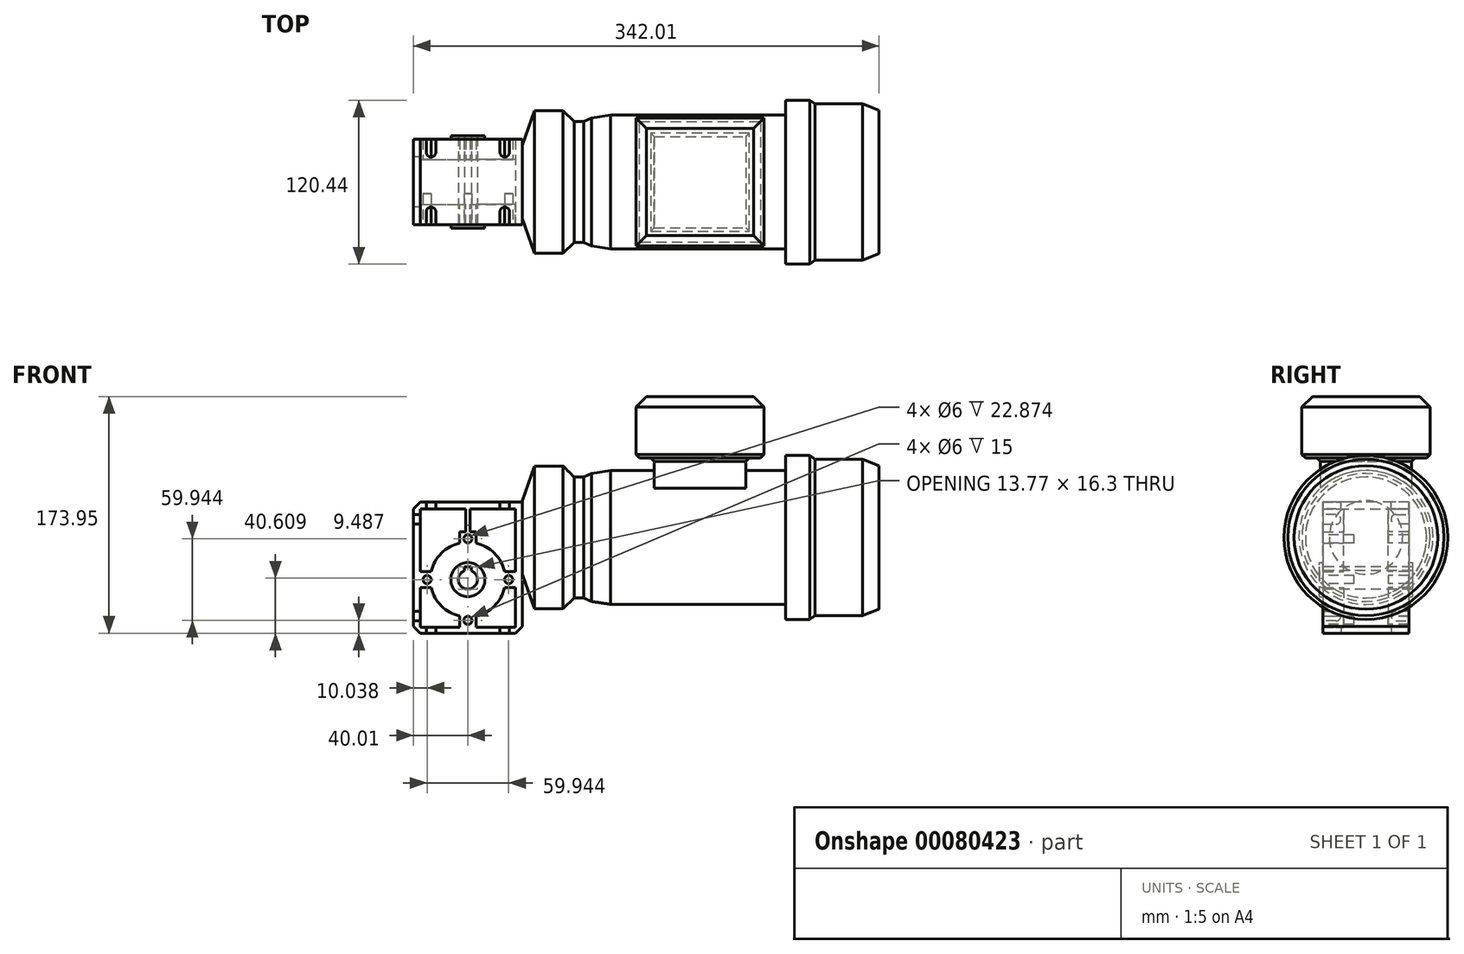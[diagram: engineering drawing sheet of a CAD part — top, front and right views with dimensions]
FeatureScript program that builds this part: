
annotation { "Feature Type Name" : "Feature", "Feature Type Description" : "" }
export const myFeature = defineFeature(function(context is Context, id is Id, definition is map)
    precondition{}
    {
        {
            var Q0;
            Q0=qCreatedBy(makeId("Top.planeOp"),FACE);
            var sketch = newSketch(context, id + "F0", { "sketchPlane" : qUnion([Q0])});
            skLineSegment(sketch, "E0.bottom", {"start": v(-40, 16.5) * mm, "end": v(40, 16.5) * mm});
            skLineSegment(sketch, "E0.top", {"start": v(-40, -16.5) * mm, "end": v(40, -16.5) * mm});
            skLineSegment(sketch, "E0.left", {"start": v(-40, 16.5) * mm, "end": v(-40, -16.5) * mm});
            skLineSegment(sketch, "E0.right", {"start": v(40, 16.5) * mm, "end": v(40, -16.5) * mm});
            skPoint(sketch, "E0.middle", {"position": v(0, 0) * mm});
            skSolve(sketch);
        }
        {
            var Q0;
            Q0 = qSketchRegion(id + "F0", true);
            extrude(context, id + "F1", {"entities" : qUnion([Q0]), "endBound" : BoundingType.SYMMETRIC, "depth" : 96.35 * mm});
        }
        {
            var Q0;
            Q0=makeQuery(id+"F1.opExtrude","SWEPT_FACE",FACE,{"disambiguationData":[OSD([sQuery(id+"F0.wireOp",EDGE,"E0.top")])]});
            var sketch = newSketch(context, id + "F2", { "sketchPlane" : qUnion([Q0])});
            skArc(sketch, "E1", {"start": v(-2.5, -2.18) * mm, "mid": v(0, -15.72) * mm, "end": v(2.5, -2.18) * mm});
            skLineSegment(sketch, "E2", {"start": v(-2.5, -2.18) * mm, "end": v(-2.5, 0.58) * mm});
            skLineSegment(sketch, "E3", {"start": v(-2.5, 0.58) * mm, "end": v(2.5, 0.58) * mm});
            skLineSegment(sketch, "E4", {"start": v(2.5, 0.58) * mm, "end": v(2.5, -2.18) * mm});
            skPoint(sketch, "E5", {"position": v(0, -15.72) * mm});
            skSolve(sketch);
        }
        {
            var Q0;
            Q0 = qSketchRegion(id + "F2", true);
            extrude(context, id + "F3", {"entities" : qUnion([Q0]), "operationType" : NewBodyOperationType.REMOVE, "endBound" : BoundingType.UP_TO_NEXT, "oppositeDirection" : true, "depth" : 25.4 * mm});
        }
        {
            var Q0;
            Q0=qCreatedBy(makeId("Front.planeOp"),FACE);
            var sketch = newSketch(context, id + "F4", { "sketchPlane" : qUnion([Q0])});
            skCircle(sketch, "E6", {"center": v(0, -8.72) * mm, "radius": 12.5 * mm});
            skArc(sketch, "E7.0", {"start": v(-2.5, -2.18) * mm, "mid": v(0, -15.72) * mm, "end": v(2.5, -2.18) * mm});
            skLineSegment(sketch, "E8.0", {"start": v(2.5, 0.58) * mm, "end": v(2.5, -2.18) * mm});
            skLineSegment(sketch, "E9.0", {"start": v(-2.5, 0.58) * mm, "end": v(2.5, 0.58) * mm});
            skLineSegment(sketch, "E10.0", {"start": v(-2.5, -2.18) * mm, "end": v(-2.5, 0.58) * mm});
            skSolve(sketch);
        }
        {
            var Q0;
            Q0 = qSketchRegion(id + "F4", true);
            extrude(context, id + "F5", {"entities" : qUnion([Q0]), "operationType" : NewBodyOperationType.ADD, "endBound" : BoundingType.SYMMETRIC, "depth" : 68.07 * mm});
        }
        {
            var Q0;
            Q0=makeQuery(id+"F1.opExtrude","SWEPT_FACE",FACE,{"disambiguationData":[OSD([sQuery(id+"F0.wireOp",EDGE,"E0.top")])]});
            var sketch = newSketch(context, id + "F6", { "sketchPlane" : qUnion([Q0])});
            skCircle(sketch, "E11", {"center": v(0, 21.25) * mm, "radius": 3 * mm});
            skPoint(sketch, "E12", {"position": v(0, -8.72) * mm});
            skCircle(sketch, "E13.1.0", {"center": v(-29.97, -8.72) * mm, "radius": 3 * mm});
            skCircle(sketch, "E13.2.0", {"center": v(0, -38.7) * mm, "radius": 3 * mm});
            skCircle(sketch, "E13.3.0", {"center": v(29.97, -8.72) * mm, "radius": 3 * mm});
            skSolve(sketch);
        }
        {
            var Q0;
            Q0 = qSketchRegion(id + "F6", true);
            extrude(context, id + "F7", {"entities" : qUnion([Q0]), "operationType" : NewBodyOperationType.REMOVE, "oppositeDirection" : true, "depth" : 7.87 * mm});
        }
        {
            var Q0;
            Q0=makeQuery(id+"F1.opExtrude","SWEPT_FACE",FACE,{"disambiguationData":[OSD([sQuery(id+"F0.wireOp",EDGE,"E0.top")])]});
            var sketch = newSketch(context, id + "F8", { "sketchPlane" : qUnion([Q0])});
            skLineSegment(sketch, "E14", {"start": v(-6, 18.12) * mm, "end": v(-6, 26.28) * mm});
            skLineSegment(sketch, "E15", {"start": v(-6, 26.28) * mm, "end": v(6, 26.28) * mm});
            skLineSegment(sketch, "E16", {"start": v(6, 26.28) * mm, "end": v(6, 18.12) * mm});
            skArc(sketch, "E17", {"start": v(-6, 18.12) * mm, "mid": v(-19.45, 10.72) * mm, "end": v(-26.84, -2.72) * mm});
            skArc(sketch, "E18", {"start": v(6, 18.12) * mm, "mid": v(0, 18.78) * mm, "end": v(-6, 18.12) * mm, "construction": true});
            skLineSegment(sketch, "E19", {"start": v(-6, -35.56) * mm, "end": v(-6, -35.56) * mm});
            skLineSegment(sketch, "E20", {"start": v(-6, -43.72) * mm, "end": v(6, -43.72) * mm});
            skLineSegment(sketch, "E21", {"start": v(6, -43.72) * mm, "end": v(6, -35.56) * mm});
            skLineSegment(sketch, "E22", {"start": v(-6, -35.56) * mm, "end": v(-6, -43.72) * mm});
            skArc(sketch, "E23", {"start": v(-6, -35.56) * mm, "mid": v(0, -36.22) * mm, "end": v(6, -35.56) * mm, "construction": true});
            skArc(sketch, "E24", {"start": v(6, -35.56) * mm, "mid": v(19.45, -28.17) * mm, "end": v(26.84, -14.72) * mm});
            skLineSegment(sketch, "E25", {"start": v(-35, -2.72) * mm, "end": v(-35, -14.72) * mm});
            skLineSegment(sketch, "E26", {"start": v(-35, -14.72) * mm, "end": v(-26.84, -14.72) * mm});
            skLineSegment(sketch, "E27", {"start": v(26.84, -2.72) * mm, "end": v(35, -2.72) * mm});
            skLineSegment(sketch, "E28", {"start": v(35, -2.72) * mm, "end": v(35, -14.72) * mm});
            skLineSegment(sketch, "E29", {"start": v(35, -14.72) * mm, "end": v(26.84, -14.72) * mm});
            skLineSegment(sketch, "E30", {"start": v(-35, -2.72) * mm, "end": v(-26.84, -2.72) * mm});
            skArc(sketch, "E31", {"start": v(-26.84, -2.72) * mm, "mid": v(-27.5, -8.72) * mm, "end": v(-26.84, -14.72) * mm, "construction": true});
            skArc(sketch, "E32", {"start": v(-26.84, -14.72) * mm, "mid": v(-19.45, -28.17) * mm, "end": v(-6, -35.56) * mm});
            skArc(sketch, "E33", {"start": v(26.84, -14.72) * mm, "mid": v(27.5, -8.72) * mm, "end": v(26.84, -2.72) * mm, "construction": true});
            skArc(sketch, "E34", {"start": v(26.84, -2.72) * mm, "mid": v(19.45, 10.72) * mm, "end": v(6, 18.12) * mm});
            skLineSegment(sketch, "E35", {"start": v(-35, -2.72) * mm, "end": v(-35, 43.17) * mm});
            skLineSegment(sketch, "E36", {"start": v(-35, 43.17) * mm, "end": v(-1.5, 43.17) * mm});
            skLineSegment(sketch, "E37", {"start": v(-1.5, 43.17) * mm, "end": v(-1.5, 26.28) * mm});
            skLineSegment(sketch, "E38", {"start": v(1.5, 26.28) * mm, "end": v(1.5, 43.17) * mm});
            skLineSegment(sketch, "E39", {"start": v(1.5, 43.17) * mm, "end": v(35, 43.17) * mm});
            skLineSegment(sketch, "E40", {"start": v(35, 43.17) * mm, "end": v(35, -2.72) * mm});
            skLineSegment(sketch, "E41", {"start": v(35, -14.72) * mm, "end": v(35, -43.72) * mm});
            skLineSegment(sketch, "E42", {"start": v(35, -43.72) * mm, "end": v(6, -43.72) * mm});
            skLineSegment(sketch, "E43", {"start": v(-35, -14.72) * mm, "end": v(-35, -43.72) * mm});
            skLineSegment(sketch, "E44", {"start": v(-35, -43.72) * mm, "end": v(-6, -43.72) * mm});
            skLineSegment(sketch, "E45", {"start": v(-35, 43.17) * mm, "end": v(-40, 43.17) * mm, "construction": true});
            skLineSegment(sketch, "E46", {"start": v(-35, 43.17) * mm, "end": v(-35, 48.17) * mm, "construction": true});
            skSolve(sketch);
        }
        {
            var Q0;
            Q0=makeQuery(id+"F8.imprint","IMPRINT",FACE,{"disambiguationData":[TD([[makeQuery(id+"F8.imprint","IMPRINT",EDGE,{"derivedFrom":sQuery(id+"F8.wireOp",EDGE,"E20")}),-1.0]])]});
            var Q1;
            {var subQ4=sQuery(id+"F8.wireOp",EDGE,"E14");Q1=makeQuery(id+"F8.imprint","IMPRINT",FACE,{"disambiguationData":[TD([[makeQuery(id+"F8.imprint","IMPRINT",EDGE,{"derivedFrom":subQ4}),-1.0]])]});}
            extrude(context, id + "F9", {"entities" : qUnion([Q0, Q1]), "depth" : 15 * mm});
        }
        {
            var Q0;
            Q0=makeQuery(id+"F9.opExtrude","SWEPT_BODY",BODY,{"disambiguationData":[OSD([sQuery(id+"F0.wireOp",EDGE,"E0.top"),sQuery(id+"F0.wireOp",EDGE,"E0.left"),sQuery(id+"F0.wireOp",EDGE,"E0.right"),sQuery(id+"F4.wireOp",EDGE,"E6"),sQuery(id+"F6.wireOp",EDGE,"E11"),sQuery(id+"F6.wireOp",EDGE,"E13.1.0"),sQuery(id+"F6.wireOp",EDGE,"E13.2.0"),sQuery(id+"F6.wireOp",EDGE,"E13.3.0"),sQuery(id+"F8.wireOp",EDGE,"E14"),sQuery(id+"F8.wireOp",EDGE,"E15"),sQuery(id+"F8.wireOp",EDGE,"E16"),sQuery(id+"F8.wireOp",EDGE,"E17"),sQuery(id+"F8.wireOp",EDGE,"E21"),sQuery(id+"F8.wireOp",EDGE,"E22"),sQuery(id+"F8.wireOp",EDGE,"E24"),sQuery(id+"F8.wireOp",EDGE,"E26"),sQuery(id+"F8.wireOp",EDGE,"E27"),sQuery(id+"F8.wireOp",EDGE,"E29"),sQuery(id+"F8.wireOp",EDGE,"E30"),sQuery(id+"F8.wireOp",EDGE,"E32"),sQuery(id+"F8.wireOp",EDGE,"E34"),sQuery(id+"F8.wireOp",EDGE,"E35"),sQuery(id+"F8.wireOp",EDGE,"E36"),sQuery(id+"F8.wireOp",EDGE,"E37"),sQuery(id+"F8.wireOp",EDGE,"E38"),sQuery(id+"F8.wireOp",EDGE,"E39"),sQuery(id+"F8.wireOp",EDGE,"E40"),sQuery(id+"F8.wireOp",EDGE,"E41"),sQuery(id+"F8.wireOp",EDGE,"E42"),sQuery(id+"F8.wireOp",EDGE,"E43"),sQuery(id+"F8.wireOp",EDGE,"E44")])]});
            var Q1;
            Q1=qCreatedBy(makeId("Front.planeOp"),FACE);
            mirror(context, id + "F10", {"operationType" : NewBodyOperationType.ADD, "entities" : qUnion([Q0]), "mirrorPlane" : qUnion([Q1])});
        }
        {
            var Q0;
            {var subQ0=sQuery(id+"F0.wireOp",EDGE,"E0.top");var subQ1=makeQuery(id+"F9.opExtrude","SWEPT_FACE",FACE,{"disambiguationData":[OSD([subQ0]),TDD([makeQuery(id+"F8.imprint","IMPRINT",EDGE,{"derivedFrom":makeQuery(id+"F1.opExtrude","CAP_EDGE",EDGE,{"disambiguationData":[OSD([subQ0])],"isStart":false})})])]});Q0=makeQuery(id+"F10.boolean.opBoolean","MERGE",FACE,{"derivedFrom":[makeQuery(id+"F1.opExtrude","CAP_FACE",FACE,{"disambiguationData":[OSD([sQuery(id+"F0.wireOp",EDGE,"E0.bottom"),subQ0,sQuery(id+"F0.wireOp",EDGE,"E0.left"),sQuery(id+"F0.wireOp",EDGE,"E0.right")])],"isStart":false}),subQ1,makeQuery(id+"F10.opPattern","COPY",FACE,{"derivedFrom":subQ1,"instanceName":"1"})]});}
            var sketch = newSketch(context, id + "F11", { "sketchPlane" : qUnion([Q0])});
            skLineSegment(sketch, "E47", {"start": v(-30.6, -31.5) * mm, "end": v(-30.6, -21.97) * mm});
            skLineSegment(sketch, "E48", {"start": v(-23.5, -31.5) * mm, "end": v(-23.5, -21.97) * mm});
            skArc(sketch, "E49", {"start": v(-30.6, -21.97) * mm, "mid": v(-27.05, -18.41) * mm, "end": v(-23.5, -21.97) * mm});
            skLineSegment(sketch, "E50", {"start": v(-30.6, -31.5) * mm, "end": v(-23.5, -31.5) * mm});
            skArc(sketch, "E51.MirrorCS", {"start": v(30.6, -21.97) * mm, "mid": v(27.05, -18.41) * mm, "end": v(23.5, -21.97) * mm});
            skLineSegment(sketch, "E52.MirrorCS", {"start": v(23.5, -31.5) * mm, "end": v(23.5, -21.97) * mm});
            skLineSegment(sketch, "E53.MirrorCS", {"start": v(30.6, -31.5) * mm, "end": v(30.6, -21.97) * mm});
            skLineSegment(sketch, "E54.MirrorCS", {"start": v(30.6, -31.5) * mm, "end": v(23.5, -31.5) * mm});
            skArc(sketch, "E55.MirrorCS", {"start": v(-30.6, 21.97) * mm, "mid": v(-27.05, 18.41) * mm, "end": v(-23.5, 21.97) * mm});
            skLineSegment(sketch, "E56.MirrorCS", {"start": v(-30.6, 31.5) * mm, "end": v(-30.6, 21.97) * mm});
            skLineSegment(sketch, "E57.MirrorCS", {"start": v(-23.5, 31.5) * mm, "end": v(-23.5, 21.97) * mm});
            skLineSegment(sketch, "E58.MirrorCS", {"start": v(-30.6, 31.5) * mm, "end": v(-23.5, 31.5) * mm});
            skLineSegment(sketch, "E59.MirrorCS", {"start": v(30.6, 31.5) * mm, "end": v(23.5, 31.5) * mm});
            skLineSegment(sketch, "E60.MirrorCS", {"start": v(23.5, 31.5) * mm, "end": v(23.5, 21.97) * mm});
            skArc(sketch, "E61.MirrorCS", {"start": v(30.6, 21.97) * mm, "mid": v(27.05, 18.41) * mm, "end": v(23.5, 21.97) * mm});
            skLineSegment(sketch, "E62.MirrorCS", {"start": v(30.6, 31.5) * mm, "end": v(30.6, 21.97) * mm});
            skSolve(sketch);
        }
        {
            var Q0;
            Q0 = qSketchRegion(id + "F11", true);
            extrude(context, id + "F12", {"entities" : qUnion([Q0]), "operationType" : NewBodyOperationType.REMOVE, "endBound" : BoundingType.UP_TO_NEXT, "oppositeDirection" : true, "depth" : 114.3 * mm});
        }
        {
            var Q0;
            {var subQ0=sQuery(id+"F0.wireOp",EDGE,"E0.top");var subQ1=makeQuery(id+"F9.opExtrude","SWEPT_FACE",FACE,{"disambiguationData":[OSD([subQ0]),TDD([makeQuery(id+"F8.imprint","IMPRINT",EDGE,{"derivedFrom":makeQuery(id+"F1.opExtrude","CAP_EDGE",EDGE,{"disambiguationData":[OSD([subQ0])],"isStart":true})})])]});Q0=makeQuery(id+"F10.boolean.opBoolean","MERGE",FACE,{"derivedFrom":[makeQuery(id+"F1.opExtrude","CAP_FACE",FACE,{"disambiguationData":[OSD([sQuery(id+"F0.wireOp",EDGE,"E0.bottom"),subQ0,sQuery(id+"F0.wireOp",EDGE,"E0.left"),sQuery(id+"F0.wireOp",EDGE,"E0.right")])],"isStart":true}),subQ1,makeQuery(id+"F10.opPattern","COPY",FACE,{"derivedFrom":subQ1,"instanceName":"1"})]});}
            var sketch = newSketch(context, id + "F13", { "sketchPlane" : qUnion([Q0])});
            skLineSegment(sketch, "E63.0", {"start": v(-23.5, 21.97) * mm, "end": v(-23.5, 31.5) * mm});
            skArc(sketch, "E64.0", {"start": v(-23.5, 21.97) * mm, "mid": v(-27.05, 18.41) * mm, "end": v(-30.6, 21.97) * mm});
            skLineSegment(sketch, "E65.0", {"start": v(-30.6, 21.97) * mm, "end": v(-30.6, 31.5) * mm});
            skLineSegment(sketch, "E66.0", {"start": v(23.5, 21.97) * mm, "end": v(23.5, 31.5) * mm});
            skArc(sketch, "E67.0", {"start": v(23.5, 21.97) * mm, "mid": v(27.05, 18.41) * mm, "end": v(30.6, 21.97) * mm});
            skLineSegment(sketch, "E68.0", {"start": v(30.6, 21.97) * mm, "end": v(30.6, 31.5) * mm});
            skLineSegment(sketch, "E69", {"start": v(-30.6, 31.5) * mm, "end": v(-23.5, 31.5) * mm});
            skLineSegment(sketch, "E70", {"start": v(23.5, 31.5) * mm, "end": v(30.6, 31.5) * mm});
            skLineSegment(sketch, "E71.MirrorCS", {"start": v(23.5, -21.97) * mm, "end": v(23.5, -31.5) * mm});
            skArc(sketch, "E72.MirrorCS", {"start": v(23.5, -21.97) * mm, "mid": v(27.05, -18.41) * mm, "end": v(30.6, -21.97) * mm});
            skLineSegment(sketch, "E73.MirrorCS", {"start": v(30.6, -21.97) * mm, "end": v(30.6, -31.5) * mm});
            skLineSegment(sketch, "E74.MirrorCS", {"start": v(23.5, -31.5) * mm, "end": v(30.6, -31.5) * mm});
            skLineSegment(sketch, "E75.MirrorCS", {"start": v(-30.6, -31.5) * mm, "end": v(-23.5, -31.5) * mm});
            skLineSegment(sketch, "E76.MirrorCS", {"start": v(-30.6, -21.97) * mm, "end": v(-30.6, -31.5) * mm});
            skArc(sketch, "E77.MirrorCS", {"start": v(-23.5, -21.97) * mm, "mid": v(-27.05, -18.41) * mm, "end": v(-30.6, -21.97) * mm});
            skLineSegment(sketch, "E78.MirrorCS", {"start": v(-23.5, -21.97) * mm, "end": v(-23.5, -31.5) * mm});
            skSolve(sketch);
        }
        {
            var Q0;
            Q0 = qSketchRegion(id + "F13", true);
            extrude(context, id + "F14", {"entities" : qUnion([Q0]), "operationType" : NewBodyOperationType.REMOVE, "endBound" : BoundingType.UP_TO_NEXT, "oppositeDirection" : true, "depth" : 25.4 * mm});
        }
        {
            var Q0;
            {var subQ0=sQuery(id+"F0.wireOp",EDGE,"E0.left");var subQ1=makeQuery(id+"F9.opExtrude","SWEPT_FACE",FACE,{"disambiguationData":[OSD([sQuery(id+"F0.wireOp",EDGE,"E0.top"),subQ0])]});Q0=makeQuery(id+"F10.boolean.opBoolean","MERGE",FACE,{"derivedFrom":[makeQuery(id+"F1.opExtrude","SWEPT_FACE",FACE,{"disambiguationData":[OSD([subQ0])]}),subQ1,makeQuery(id+"F10.opPattern","COPY",FACE,{"derivedFrom":subQ1,"instanceName":"1"})]});}
            var sketch = newSketch(context, id + "F15", { "sketchPlane" : qUnion([Q0])});
            skLineSegment(sketch, "E79", {"start": v(31.5, 39.12) * mm, "end": v(31.5, 32) * mm});
            skArc(sketch, "E80.MirrorCS", {"start": v(21.97, 39.12) * mm, "mid": v(18.42, 35.56) * mm, "end": v(21.97, 32) * mm});
            skLineSegment(sketch, "E81", {"start": v(21.97, 39.12) * mm, "end": v(31.5, 39.12) * mm});
            skLineSegment(sketch, "E82", {"start": v(31.5, 32) * mm, "end": v(21.97, 32) * mm});
            skArc(sketch, "E83.MirrorCS", {"start": v(-21.97, 39.12) * mm, "mid": v(-18.41, 35.56) * mm, "end": v(-21.97, 32) * mm});
            skLineSegment(sketch, "E84.MirrorCS", {"start": v(-21.97, 39.12) * mm, "end": v(-31.5, 39.12) * mm});
            skLineSegment(sketch, "E85.MirrorCS", {"start": v(-31.5, 32) * mm, "end": v(-21.97, 32) * mm});
            skLineSegment(sketch, "E86.MirrorCS", {"start": v(-31.5, 39.12) * mm, "end": v(-31.5, 32) * mm});
            skLineSegment(sketch, "E87.MirrorCS", {"start": v(-31.5, -39.12) * mm, "end": v(-31.5, -32) * mm});
            skLineSegment(sketch, "E88.MirrorCS", {"start": v(-31.5, -32) * mm, "end": v(-21.97, -32) * mm});
            skArc(sketch, "E89.MirrorCS", {"start": v(-21.97, -39.12) * mm, "mid": v(-18.41, -35.56) * mm, "end": v(-21.97, -32) * mm});
            skLineSegment(sketch, "E90.MirrorCS", {"start": v(-21.97, -39.12) * mm, "end": v(-31.5, -39.12) * mm});
            skArc(sketch, "E91.MirrorCS", {"start": v(21.97, -39.12) * mm, "mid": v(18.42, -35.56) * mm, "end": v(21.97, -32) * mm});
            skLineSegment(sketch, "E92.MirrorCS", {"start": v(31.5, -32) * mm, "end": v(21.97, -32) * mm});
            skLineSegment(sketch, "E93.MirrorCS", {"start": v(31.5, -39.12) * mm, "end": v(31.5, -32) * mm});
            skLineSegment(sketch, "E94.MirrorCS", {"start": v(21.97, -39.12) * mm, "end": v(31.5, -39.12) * mm});
            skSolve(sketch);
        }
        {
            var Q0;
            Q0 = qSketchRegion(id + "F15", true);
            extrude(context, id + "F16", {"entities" : qUnion([Q0]), "operationType" : NewBodyOperationType.REMOVE, "endBound" : BoundingType.UP_TO_NEXT, "oppositeDirection" : true, "depth" : 25.4 * mm});
        }
        {
            var Q0;
            {var subQ0=sQuery(id+"F0.wireOp",EDGE,"E0.right");var subQ1=makeQuery(id+"F9.opExtrude","SWEPT_FACE",FACE,{"disambiguationData":[OSD([sQuery(id+"F0.wireOp",EDGE,"E0.top"),subQ0])]});Q0=makeQuery(id+"F10.boolean.opBoolean","MERGE",FACE,{"derivedFrom":[makeQuery(id+"F1.opExtrude","SWEPT_FACE",FACE,{"disambiguationData":[OSD([subQ0])]}),subQ1,makeQuery(id+"F10.opPattern","COPY",FACE,{"derivedFrom":subQ1,"instanceName":"1"})]});}
            var sketch = newSketch(context, id + "F17", { "sketchPlane" : qUnion([Q0])});
            skLineSegment(sketch, "E95.0", {"start": v(-8.62, -11.72) * mm, "end": v(-8.62, -5.72) * mm, "construction": true});
            skPoint(sketch, "E96", {"position": v(-8.62, -8.72) * mm});
            skCircle(sketch, "E97", {"center": v(0, 22.27) * mm, "radius": 27 * mm});
            skSolve(sketch);
        }
        {
            var Q0;
            {var subQ0=sQuery(id+"F0.wireOp",EDGE,"E0.left");var subQ1=makeQuery(id+"F9.opExtrude","SWEPT_FACE",FACE,{"disambiguationData":[OSD([sQuery(id+"F0.wireOp",EDGE,"E0.top"),subQ0])]});Q0=makeQuery(id+"F10.boolean.opBoolean","MERGE",FACE,{"derivedFrom":[makeQuery(id+"F1.opExtrude","SWEPT_FACE",FACE,{"disambiguationData":[OSD([subQ0])]}),subQ1,makeQuery(id+"F10.opPattern","COPY",FACE,{"derivedFrom":subQ1,"instanceName":"1"})]});}
            cPlane(context, id + "F18", {"entities" : qUnion([Q0]), "cplaneType" : CPlaneType.OFFSET, "offset" : 89 * mm, "oppositeDirection" : true, "width" : 152.4 * mm, "height" : 152.4 * mm});
        }
        {
            var Q0;
            Q0=qCreatedBy(id+"F18.planeOp",FACE);
            var sketch = newSketch(context, id + "F19", { "sketchPlane" : qUnion([Q0])});
            skCircle(sketch, "E98", {"center": v(0, 22.27) * mm, "radius": 52.45 * mm});
            skSolve(sketch);
        }
        {
            var Q1;
            Q1 = qSketchRegion(id + "F17", true);
            var Q2;
            Q2 = qSketchRegion(id + "F19", true);
            loft(context, id + "F20", {"operationType" : NewBodyOperationType.ADD, "sheetProfilesArray" : [{ "sheetProfileEntities" : qUnion([Q1]) }, { "sheetProfileEntities" : qUnion([Q2]) }]});
        }
        {
            var Q0;
            Q0 = qSketchRegion(id + "F19", true);
            extrude(context, id + "F21", {"entities" : qUnion([Q0]), "operationType" : NewBodyOperationType.ADD, "oppositeDirection" : true, "depth" : 21 * mm});
        }
        {
            var Q0;
            Q0=makeQuery(id+"F21.opExtrude","CAP_FACE",FACE,{"disambiguationData":[OSD([sQuery(id+"F19.wireOp",EDGE,"E98")])],"isStart":false});
            cPlane(context, id + "F22", {"entities" : qUnion([Q0]), "cplaneType" : CPlaneType.OFFSET, "offset" : 8 * mm, "width" : 152.4 * mm, "height" : 152.4 * mm});
        }
        {
            var Q0;
            Q0=qCreatedBy(id+"F22.planeOp",FACE);
            var sketch = newSketch(context, id + "F23", { "sketchPlane" : qUnion([Q0])});
            skCircle(sketch, "E99", {"center": v(0, 22.27) * mm, "radius": 44.45 * mm});
            skSolve(sketch);
        }
        {
            var Q1;
            Q1=makeQuery(id+"F21.opExtrude","CAP_FACE",FACE,{"disambiguationData":[OSD([sQuery(id+"F19.wireOp",EDGE,"E98")])],"isStart":false});
            var Q2;
            Q2=makeQuery(id+"F23.imprint","IMPRINT",FACE,{"disambiguationData":[TD([[makeQuery(id+"F23.imprint","IMPRINT",EDGE,{"derivedFrom":sQuery(id+"F23.wireOp",EDGE,"E99")}),1.0]])]});
            loft(context, id + "F24", {"operationType" : NewBodyOperationType.ADD, "sheetProfilesArray" : [{ "sheetProfileEntities" : qUnion([Q1]) }, { "sheetProfileEntities" : qUnion([Q2]) }]});
        }
        {
            var Q0;
            Q0=qCreatedBy(makeId("Front.planeOp"),FACE);
            var sketch = newSketch(context, id + "F25", { "sketchPlane" : qUnion([Q0])});
            skLineSegment(sketch, "E100.0", {"start": v(78, 66.72) * mm, "end": v(78, -22.18) * mm, "construction": true});
            skPoint(sketch, "E101", {"position": v(78, 22.27) * mm});
            skLineSegment(sketch, "E102", {"start": v(78, 66.72) * mm, "end": v(84.97, 66.72) * mm});
            skLineSegment(sketch, "E103", {"start": v(84.97, 66.72) * mm, "end": v(90.65, 69.3) * mm});
            skLineSegment(sketch, "E104", {"start": v(90.65, 69.3) * mm, "end": v(104.92, 71.49) * mm});
            skLineSegment(sketch, "E105", {"start": v(104.92, 71.49) * mm, "end": v(233.25, 71.49) * mm});
            skLineSegment(sketch, "E106", {"start": v(233.25, 71.49) * mm, "end": v(233.25, 82.49) * mm});
            skLineSegment(sketch, "E107", {"start": v(233.25, 82.49) * mm, "end": v(251.25, 82.49) * mm});
            skLineSegment(sketch, "E108", {"start": v(251.25, 82.49) * mm, "end": v(255, 79.65) * mm});
            skLineSegment(sketch, "E109", {"start": v(255, 79.65) * mm, "end": v(290, 79.65) * mm});
            skLineSegment(sketch, "E110", {"start": v(290, 79.65) * mm, "end": v(302, 75.05) * mm});
            skLineSegment(sketch, "E111", {"start": v(302, 75.05) * mm, "end": v(302, 22.27) * mm});
            skLineSegment(sketch, "E112", {"start": v(302, 22.27) * mm, "end": v(78, 22.27) * mm});
            skLineSegment(sketch, "E113", {"start": v(78, 66.72) * mm, "end": v(78, 22.27) * mm});
            skSolve(sketch);
        }
        {
            var Q0;
            Q0=makeQuery(id+"F25.imprint","IMPRINT",FACE,{"disambiguationData":[TD([[makeQuery(id+"F25.imprint","IMPRINT",EDGE,{"derivedFrom":sQuery(id+"F25.wireOp",EDGE,"E102")}),-1.0]])]});
            var Q1;
            Q1=sQuery(id+"F25.wireOp",EDGE,"E112");
            revolve(context, id + "F26", {"operationType" : NewBodyOperationType.ADD, "entities" : qUnion([Q0]), "axis" : qUnion([Q1]), "revolveType" : RevolveType.FULL});
        }
        {
            var Q0;
            Q0=qCreatedBy(makeId("Top.planeOp"),FACE);
            var sketch = newSketch(context, id + "F27", { "sketchPlane" : qUnion([Q0])});
            skLineSegment(sketch, "E114.bottom", {"start": v(204, 33.5) * mm, "end": v(137, 33.5) * mm});
            skLineSegment(sketch, "E114.top", {"start": v(204, -33.5) * mm, "end": v(137, -33.5) * mm});
            skLineSegment(sketch, "E114.left", {"start": v(204, 33.5) * mm, "end": v(204, -33.5) * mm});
            skLineSegment(sketch, "E114.right", {"start": v(137, 33.5) * mm, "end": v(137, -33.5) * mm});
            skPoint(sketch, "E114.middle", {"position": v(170.5, 0) * mm});
            skSolve(sketch);
        }
        {
            var Q0;
            Q0 = qSketchRegion(id + "F27", true);
            extrude(context, id + "F28", {"entities" : qUnion([Q0]), "operationType" : NewBodyOperationType.ADD, "depth" : 80.77 * mm});
        }
        {
            var Q0;
            Q0=makeQuery(id+"F28.opExtrude","CAP_FACE",FACE,{"disambiguationData":[OSD([sQuery(id+"F27.wireOp",EDGE,"E114.bottom"),sQuery(id+"F27.wireOp",EDGE,"E114.top"),sQuery(id+"F27.wireOp",EDGE,"E114.left"),sQuery(id+"F27.wireOp",EDGE,"E114.right")])],"isStart":false});
            var sketch = newSketch(context, id + "F29", { "sketchPlane" : qUnion([Q0])});
            skLineSegment(sketch, "E115.bottom", {"start": v(123.5, 47) * mm, "end": v(217.5, 47) * mm});
            skLineSegment(sketch, "E115.top", {"start": v(123.5, -47) * mm, "end": v(217.5, -47) * mm});
            skLineSegment(sketch, "E115.left", {"start": v(123.5, 47) * mm, "end": v(123.5, -47) * mm});
            skLineSegment(sketch, "E115.right", {"start": v(217.5, 47) * mm, "end": v(217.5, -47) * mm});
            skPoint(sketch, "E115.middle", {"position": v(170.5, 0) * mm});
            skPoint(sketch, "E116", {"position": v(170.5, 33.5) * mm});
            skPoint(sketch, "E117", {"position": v(170.5, 47) * mm});
            skSolve(sketch);
        }
        {
            var Q0;
            Q0 = qSketchRegion(id + "F29", true);
            extrude(context, id + "F30", {"entities" : qUnion([Q0]), "operationType" : NewBodyOperationType.ADD, "depth" : 45 * mm});
        }
        {
            var Q0;
            Q0=makeQuery(id+"F30.opExtrude","CAP_FACE",FACE,{"disambiguationData":[OSD([sQuery(id+"F29.wireOp",EDGE,"E115.bottom"),sQuery(id+"F29.wireOp",EDGE,"E115.top"),sQuery(id+"F29.wireOp",EDGE,"E115.left"),sQuery(id+"F29.wireOp",EDGE,"E115.right")])],"isStart":false});
            chamfer(context, id + "F31", {"entities" : qUnion([Q0]), "width" : 7.62 * mm, "tangentPropagation" : true});
        }
        {
            var Q0;
            Q0=makeQuery(id+"F30.opExtrude","CAP_FACE",FACE,{"disambiguationData":[OSD([sQuery(id+"F29.wireOp",EDGE,"E115.bottom"),sQuery(id+"F29.wireOp",EDGE,"E115.top"),sQuery(id+"F29.wireOp",EDGE,"E115.left"),sQuery(id+"F29.wireOp",EDGE,"E115.right")])],"isStart":true});
            chamfer(context, id + "F32", {"entities" : qUnion([Q0]), "width" : 2.54 * mm, "tangentPropagation" : true});
        }
        {
            var Q0;
            {var subQ0=sQuery(id+"F0.wireOp",EDGE,"E0.top");var subQ1=sQuery(id+"F0.wireOp",EDGE,"E0.left");var subQ2=makeQuery(id+"F9.opExtrude","SWEPT_EDGE",EDGE,{"disambiguationData":[OSD([subQ0,subQ1]),TDD([makeQuery(id+"F8.imprint","INTERSECT",VERTEX,{"derivedFrom":[makeQuery(id+"F1.opExtrude","SWEPT_EDGE",EDGE,{"disambiguationData":[OSD([subQ0,subQ1])]}),makeQuery(id+"F1.opExtrude","CAP_EDGE",EDGE,{"disambiguationData":[OSD([subQ0])],"isStart":false})]})])]});Q0=makeQuery(id+"F10.boolean.opBoolean","MERGE",EDGE,{"derivedFrom":[makeQuery(id+"F1.opExtrude","CAP_EDGE",EDGE,{"disambiguationData":[OSD([subQ1])],"isStart":false}),subQ2,makeQuery(id+"F10.opPattern","COPY",EDGE,{"derivedFrom":subQ2,"instanceName":"1"})]});}
            var Q1;
            {var subQ0=sQuery(id+"F0.wireOp",EDGE,"E0.top");var subQ1=sQuery(id+"F0.wireOp",EDGE,"E0.left");var subQ2=makeQuery(id+"F9.opExtrude","SWEPT_EDGE",EDGE,{"disambiguationData":[OSD([subQ0,subQ1]),TDD([makeQuery(id+"F8.imprint","INTERSECT",VERTEX,{"derivedFrom":[makeQuery(id+"F1.opExtrude","SWEPT_EDGE",EDGE,{"disambiguationData":[OSD([subQ0,subQ1])]}),makeQuery(id+"F1.opExtrude","CAP_EDGE",EDGE,{"disambiguationData":[OSD([subQ0])],"isStart":true})]})])]});Q1=makeQuery(id+"F10.boolean.opBoolean","MERGE",EDGE,{"derivedFrom":[makeQuery(id+"F1.opExtrude","CAP_EDGE",EDGE,{"disambiguationData":[OSD([subQ1])],"isStart":true}),subQ2,makeQuery(id+"F10.opPattern","COPY",EDGE,{"derivedFrom":subQ2,"instanceName":"1"})]});}
            var Q2;
            {var subQ0=sQuery(id+"F0.wireOp",EDGE,"E0.top");var subQ1=sQuery(id+"F0.wireOp",EDGE,"E0.right");var subQ2=makeQuery(id+"F9.opExtrude","SWEPT_EDGE",EDGE,{"disambiguationData":[OSD([subQ0,subQ1]),TDD([makeQuery(id+"F8.imprint","INTERSECT",VERTEX,{"derivedFrom":[makeQuery(id+"F1.opExtrude","SWEPT_EDGE",EDGE,{"disambiguationData":[OSD([subQ0,subQ1])]}),makeQuery(id+"F1.opExtrude","CAP_EDGE",EDGE,{"disambiguationData":[OSD([subQ0])],"isStart":true})]})])]});Q2=makeQuery(id+"F10.boolean.opBoolean","MERGE",EDGE,{"derivedFrom":[makeQuery(id+"F1.opExtrude","CAP_EDGE",EDGE,{"disambiguationData":[OSD([subQ1])],"isStart":true}),subQ2,makeQuery(id+"F10.opPattern","COPY",EDGE,{"derivedFrom":subQ2,"instanceName":"1"})]});}
            chamfer(context, id + "F33", {"entities" : qUnion([Q0, Q1, Q2]), "width" : 5.08 * mm, "tangentPropagation" : true});
        }
    });
